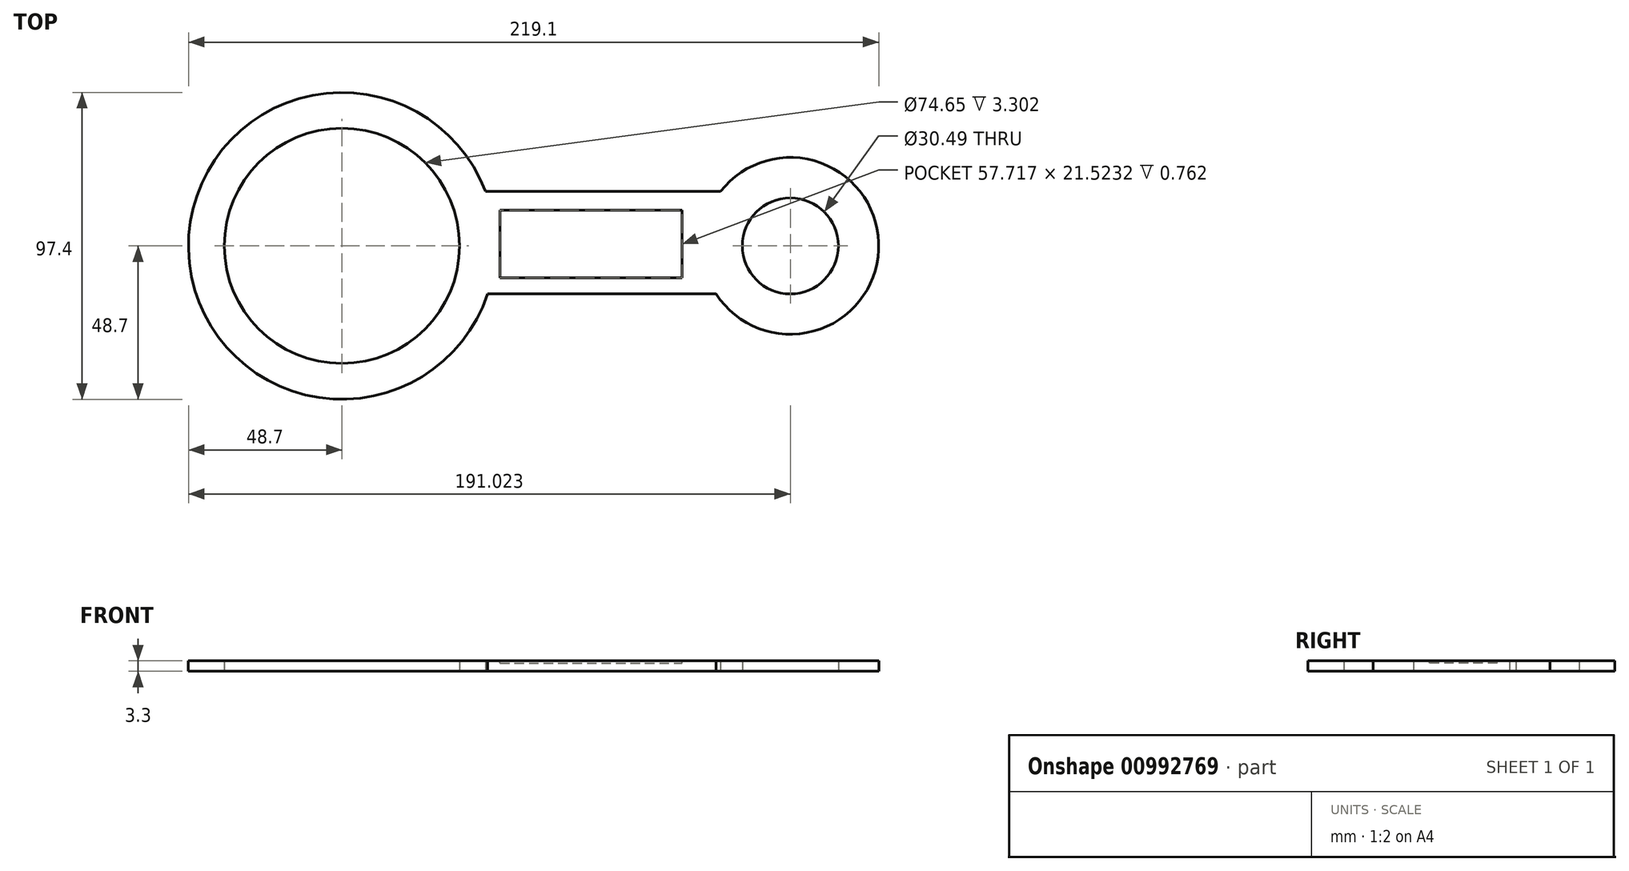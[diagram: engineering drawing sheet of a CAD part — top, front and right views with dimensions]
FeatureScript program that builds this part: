
annotation { "Feature Type Name" : "Feature", "Feature Type Description" : "" }
export const myFeature = defineFeature(function(context is Context, id is Id, definition is map)
    precondition{}
    {
        {
            var Q0;
            Q0=qCreatedBy(makeId("Top.planeOp"),FACE);
            var sketch = newSketch(context, id + "F0", { "sketchPlane" : qUnion([Q0])});
            skCircle(sketch, "E0", {"center": v(0, 0) * mm, "radius": 48.7 * mm});
            skCircle(sketch, "E1", {"center": v(142.32, 0) * mm, "radius": 28.07 * mm});
            skLineSegment(sketch, "E2", {"start": v(120.17, 17.24) * mm, "end": v(45.55, 17.24) * mm});
            skLineSegment(sketch, "E3", {"start": v(118.75, -15.24) * mm, "end": v(46.26, -15.24) * mm});
            skCircle(sketch, "E4", {"center": v(0, 0) * mm, "radius": 37.33 * mm});
            skCircle(sketch, "E5", {"center": v(142.32, 0) * mm, "radius": 15.24 * mm});
            skSolve(sketch);
        }
        {
            var Q0;
            Q0 = qSketchRegion(id + "F0", true);
            extrude(context, id + "F1", {"entities" : qUnion([Q0]), "depth" : 3.3 * mm, "offsetDistance" : 25.4 * mm});
        }
        {
            var Q0;
            Q0=makeQuery(id+"F1.opExtrude","CAP_FACE",FACE,{"disambiguationData":[OSD([sQuery(id+"F0.wireOp",EDGE,"E0"),sQuery(id+"F0.wireOp",EDGE,"E1"),sQuery(id+"F0.wireOp",EDGE,"E2"),sQuery(id+"F0.wireOp",EDGE,"E3"),sQuery(id+"F0.wireOp",EDGE,"E4"),sQuery(id+"F0.wireOp",EDGE,"E5")])],"isStart":false});
            var sketch = newSketch(context, id + "F2", { "sketchPlane" : qUnion([Q0])});
            skLineSegment(sketch, "E6.bottom", {"start": v(50.2, 11.33) * mm, "end": v(107.92, 11.33) * mm});
            skLineSegment(sketch, "E6.top", {"start": v(50.2, -10.2) * mm, "end": v(107.92, -10.2) * mm});
            skLineSegment(sketch, "E6.left", {"start": v(50.2, 11.33) * mm, "end": v(50.2, -10.2) * mm});
            skLineSegment(sketch, "E6.right", {"start": v(107.92, 11.33) * mm, "end": v(107.92, -10.2) * mm});
            skSolve(sketch);
        }
        {
            var Q0;
            Q0 = qSketchRegion(id + "F2", true);
            var Q1;
            Q1=sQuery(id+"F2.wireOp",EDGE,"E6.bottom");
            var Q2;
            Q2=sQuery(id+"F2.wireOp",EDGE,"E6.left");
            var Q3;
            Q3=sQuery(id+"F2.wireOp",EDGE,"E6.top");
            var Q4;
            Q4=sQuery(id+"F2.wireOp",EDGE,"E6.right");
            extrude(context, id + "F3", {"entities" : qUnion([Q0]), "operationType" : NewBodyOperationType.REMOVE, "surfaceEntities" : qUnion([Q1, Q2, Q3, Q4]), "oppositeDirection" : true, "depth" : 0.76 * mm, "offsetDistance" : 25.4 * mm});
        }
    });
